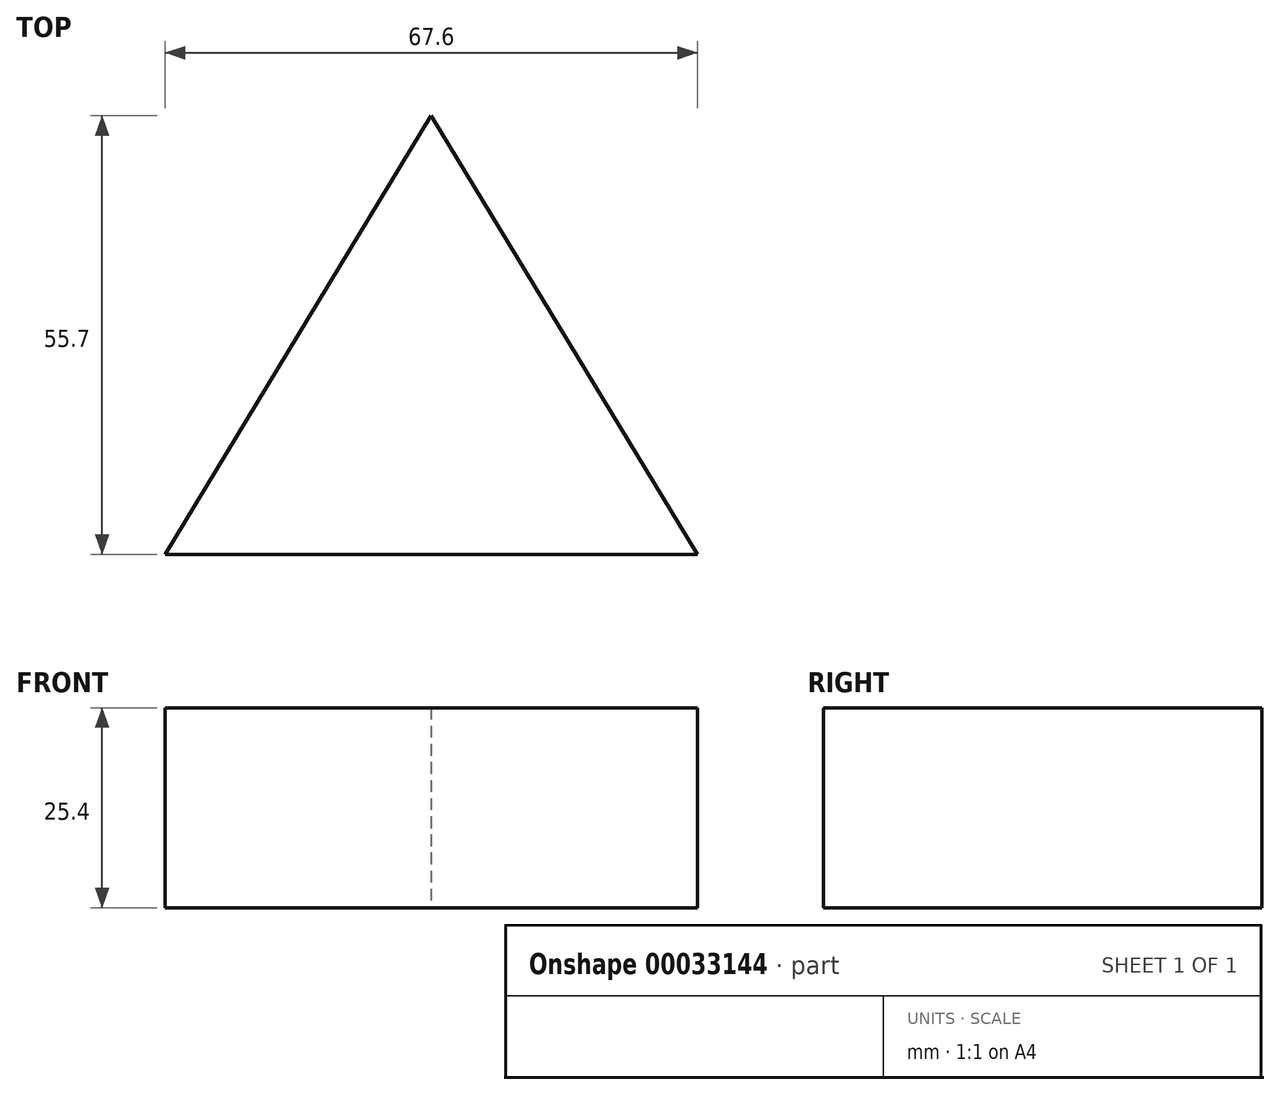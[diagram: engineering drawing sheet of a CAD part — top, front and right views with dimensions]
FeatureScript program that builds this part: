
annotation { "Feature Type Name" : "Feature", "Feature Type Description" : "" }
export const myFeature = defineFeature(function(context is Context, id is Id, definition is map)
    precondition{}
    {
        {
            var Q0;
            Q0=qCreatedBy(makeId("Top.planeOp"),FACE);
            var sketch = newSketch(context, id + "F0", { "sketchPlane" : qUnion([Q0])});
            skLineSegment(sketch, "E0", {"start": v(0, -55.7) * mm, "end": v(33.8, -55.7) * mm});
            skLineSegment(sketch, "E1", {"start": v(33.8, -55.7) * mm, "end": v(0, 0) * mm});
            skLineSegment(sketch, "E2.MirrorCS", {"start": v(-33.8, -55.7) * mm, "end": v(0, 0) * mm});
            skLineSegment(sketch, "E3.MirrorCS", {"start": v(0, -55.7) * mm, "end": v(-33.8, -55.7) * mm});
            skSolve(sketch);
        }
        {
            var Q0;
            Q0=makeQuery(id+"F0.imprint","IMPRINT",FACE,{"disambiguationData":[TD([[makeQuery(id+"F0.imprint","IMPRINT",EDGE,{"derivedFrom":sQuery(id+"F0.wireOp",EDGE,"E0")}),1.0]])]});
            extrude(context, id + "F1", {"entities" : qUnion([Q0]), "depth" : 25.4 * mm});
        }
    });
